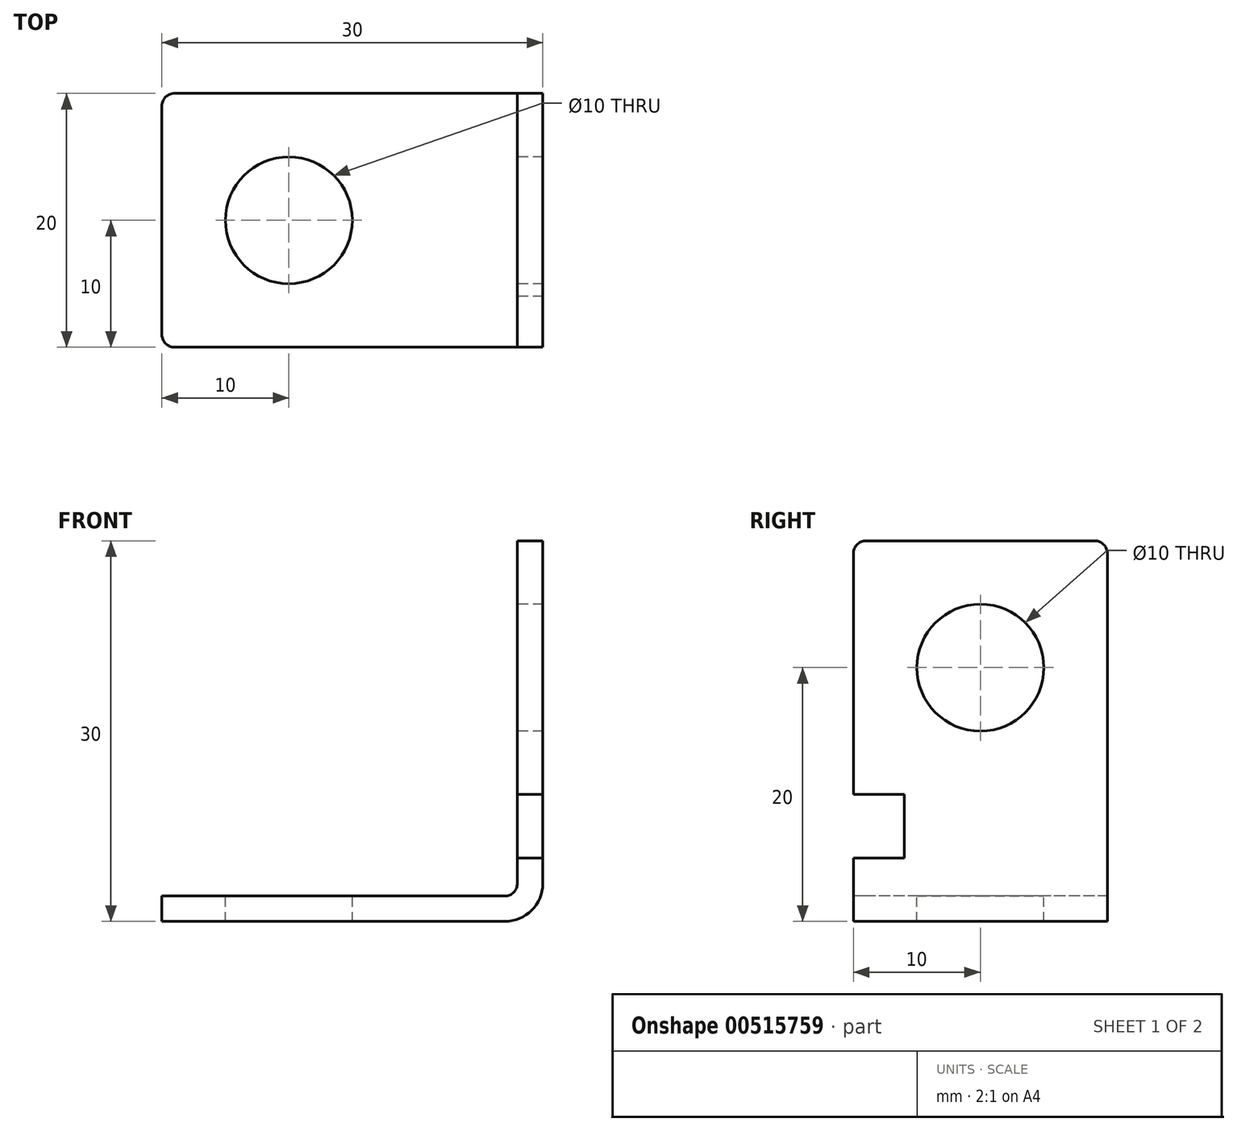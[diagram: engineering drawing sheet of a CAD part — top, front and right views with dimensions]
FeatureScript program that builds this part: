
annotation { "Feature Type Name" : "Feature", "Feature Type Description" : "" }
export const myFeature = defineFeature(function(context is Context, id is Id, definition is map)
    precondition{}
    {
        {
            var Q0;
            Q0=qCreatedBy(makeId("Front.planeOp"),FACE);
            var sketch = newSketch(context, id + "F0", { "sketchPlane" : qUnion([Q0])});
            skLineSegment(sketch, "E0", {"start": v(-30, 0) * mm, "end": v(-3, 0) * mm});
            skLineSegment(sketch, "E1", {"start": v(0, 3) * mm, "end": v(0, 30) * mm});
            skLineSegment(sketch, "E2", {"start": v(0, 30) * mm, "end": v(-2, 30) * mm});
            skLineSegment(sketch, "E3", {"start": v(-2, 30) * mm, "end": v(-2, 3) * mm});
            skLineSegment(sketch, "E4", {"start": v(-3, 2) * mm, "end": v(-30, 2) * mm});
            skLineSegment(sketch, "E5", {"start": v(-30, 2) * mm, "end": v(-30, 0) * mm});
            skPoint(sketch, "E6.visualSharp", {"position": v(-2, 2) * mm});
            skArc(sketch, "E6.filletArc", {"start": v(-3, 2) * mm, "mid": v(-2.3, 2.3) * mm, "end": v(-2, 3) * mm});
            skPoint(sketch, "E7.visualSharp", {"position": v(0, 0) * mm});
            skArc(sketch, "E7.filletArc", {"start": v(-3, 0) * mm, "mid": v(-0.88, 0.88) * mm, "end": v(0, 3) * mm});
            skSolve(sketch);
        }
        {
            var Q0;
            Q0 = qSketchRegion(id + "F0", true);
            extrude(context, id + "F1", {"entities" : qUnion([Q0]), "oppositeDirection" : true, "depth" : 20 * mm, "offsetDistance" : 25 * mm});
        }
        {
            var Q0;
            Q0=makeQuery(id+"F1.opExtrude","SWEPT_FACE",FACE,{"disambiguationData":[OSD([sQuery(id+"F0.wireOp",EDGE,"E3")])]});
            var sketch = newSketch(context, id + "F2", { "sketchPlane" : qUnion([Q0])});
            skLineSegment(sketch, "E8.bottom", {"start": v(-4, 5) * mm, "end": v(15.8, 5) * mm});
            skLineSegment(sketch, "E8.top", {"start": v(-4, 10) * mm, "end": v(15.8, 10) * mm});
            skLineSegment(sketch, "E8.left", {"start": v(-4, 5) * mm, "end": v(-4, 10) * mm});
            skLineSegment(sketch, "E8.right", {"start": v(15.8, 5) * mm, "end": v(15.8, 10) * mm});
            skSolve(sketch);
        }
        {
            var Q0;
            Q0 = qSketchRegion(id + "F2", true);
            extrude(context, id + "F3", {"entities" : qUnion([Q0]), "operationType" : NewBodyOperationType.REMOVE, "endBound" : BoundingType.THROUGH_ALL, "oppositeDirection" : true, "depth" : 25 * mm, "offsetDistance" : 25 * mm});
        }
        {
            var Q0;
            Q0=makeQuery(id+"F1.opExtrude","SWEPT_FACE",FACE,{"disambiguationData":[OSD([sQuery(id+"F0.wireOp",EDGE,"E4")])]});
            var sketch = newSketch(context, id + "F4", { "sketchPlane" : qUnion([Q0])});
            skCircle(sketch, "E9", {"center": v(-20, 10) * mm, "radius": 5 * mm});
            skSolve(sketch);
        }
        {
            var Q0;
            Q0 = qSketchRegion(id + "F4", true);
            extrude(context, id + "F5", {"entities" : qUnion([Q0]), "operationType" : NewBodyOperationType.REMOVE, "endBound" : BoundingType.THROUGH_ALL, "oppositeDirection" : true, "depth" : 25 * mm, "offsetDistance" : 25 * mm});
        }
        {
            var Q0;
            Q0=makeQuery(id+"F1.opExtrude","SWEPT_FACE",FACE,{"disambiguationData":[OSD([sQuery(id+"F0.wireOp",EDGE,"E3")])]});
            var sketch = newSketch(context, id + "F6", { "sketchPlane" : qUnion([Q0])});
            skCircle(sketch, "E10", {"center": v(-10, 20) * mm, "radius": 5 * mm});
            skSolve(sketch);
        }
        {
            var Q0;
            Q0 = qSketchRegion(id + "F6", true);
            extrude(context, id + "F7", {"entities" : qUnion([Q0]), "operationType" : NewBodyOperationType.REMOVE, "endBound" : BoundingType.THROUGH_ALL, "oppositeDirection" : true, "depth" : 25 * mm, "offsetDistance" : 25 * mm});
        }
        {
            var Q0;
            Q0=makeQuery(id+"F1.opExtrude","CAP_EDGE",EDGE,{"disambiguationData":[OSD([sQuery(id+"F0.wireOp",EDGE,"E5")])],"isStart":false});
            var Q1;
            Q1=makeQuery(id+"F1.opExtrude","CAP_EDGE",EDGE,{"disambiguationData":[OSD([sQuery(id+"F0.wireOp",EDGE,"E5")])],"isStart":true});
            var Q2;
            Q2=makeQuery(id+"F1.opExtrude","CAP_EDGE",EDGE,{"disambiguationData":[OSD([sQuery(id+"F0.wireOp",EDGE,"E2")])],"isStart":true});
            var Q3;
            Q3=makeQuery(id+"F1.opExtrude","CAP_EDGE",EDGE,{"disambiguationData":[OSD([sQuery(id+"F0.wireOp",EDGE,"E2")])],"isStart":false});
            fillet(context, id + "F8", {"entities" : qUnion([Q0, Q1, Q2, Q3]), "radius" : 1 * mm, "tangentPropagation" : true, "allowEdgeOverflow" : false});
        }
    });
